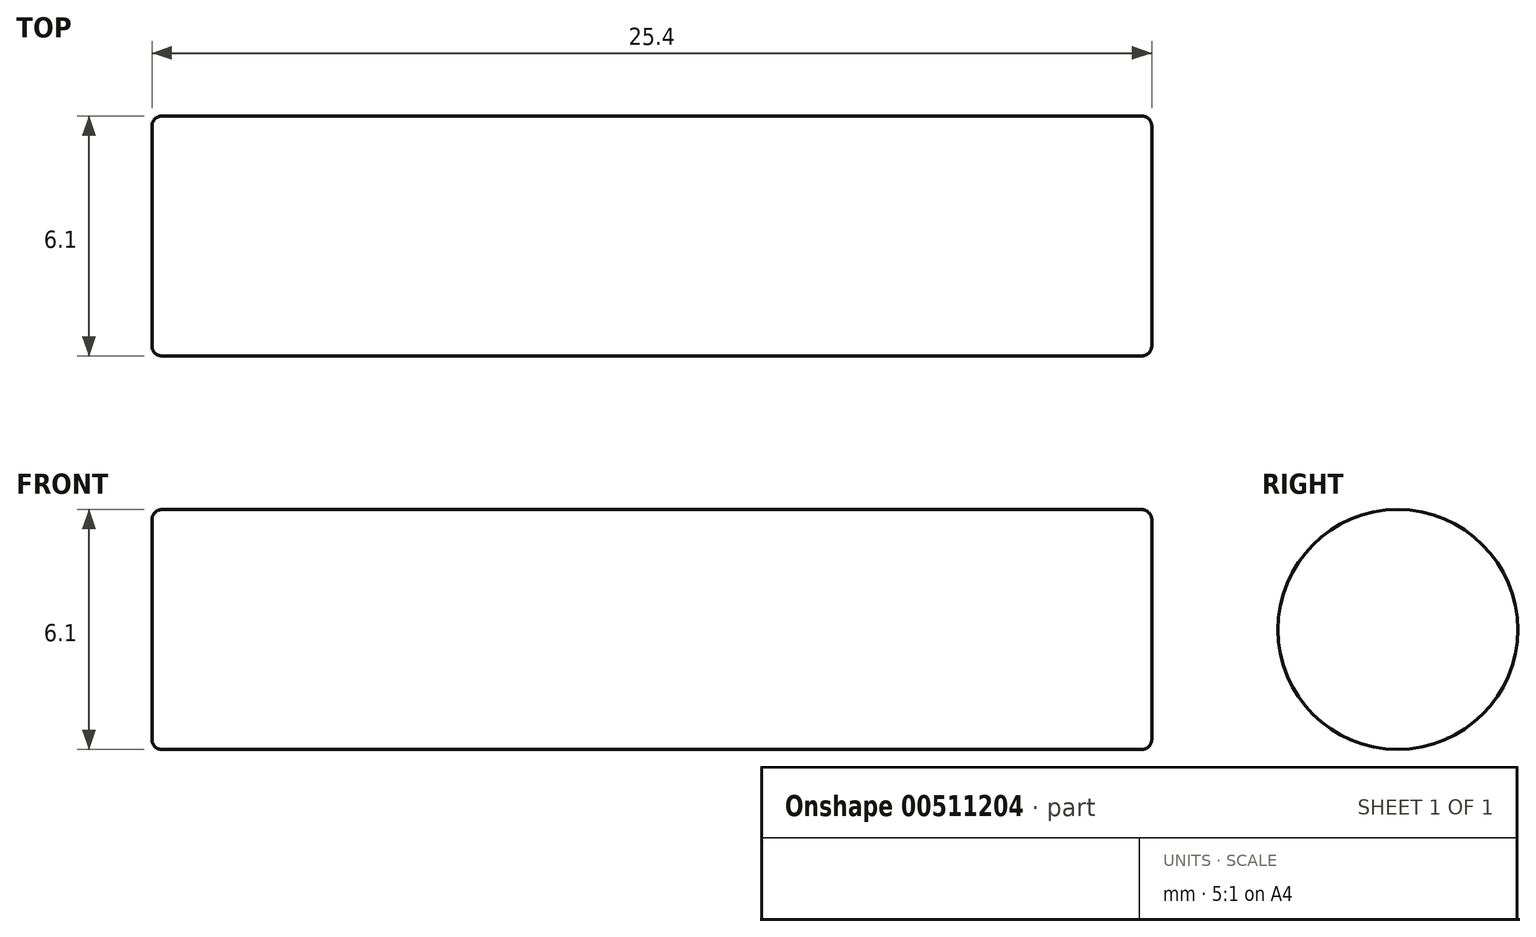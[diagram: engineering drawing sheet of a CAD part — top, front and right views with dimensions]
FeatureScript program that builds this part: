
annotation { "Feature Type Name" : "Feature", "Feature Type Description" : "" }
export const myFeature = defineFeature(function(context is Context, id is Id, definition is map)
    precondition{}
    {
        {
            var Q0;
            Q0=qCreatedBy(makeId("Right.planeOp"),FACE);
            var sketch = newSketch(context, id + "F0", { "sketchPlane" : qUnion([Q0])});
            skCircle(sketch, "E0", {"center": v(0, 0) * mm, "radius": 3.05 * mm});
            skSolve(sketch);
        }
        {
            var Q0;
            Q0=qSketchRegion(id+"F0",true);
            extrude(context, id + "F1", {"entities" : qUnion([Q0]), "depth" : 25.4 * mm});
        }
        {
            var Q0;
            Q0=makeQuery(id+"F1.opExtrude","CAP_FACE",FACE,{"disambiguationData":[OSD([sQuery(id+"F0.wireOp",EDGE,"E0")])],"isStart":false});
            var Q1;
            Q1=makeQuery(id+"F1.opExtrude","CAP_FACE",FACE,{"disambiguationData":[OSD([sQuery(id+"F0.wireOp",EDGE,"E0")])],"isStart":true});
            fillet(context, id + "F2", {"entities" : qUnion([Q0, Q1]), "radius" : 0.25 * mm, "tangentPropagation" : true, "allowEdgeOverflow" : false});
        }
    });
